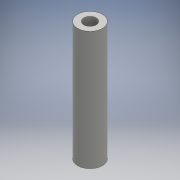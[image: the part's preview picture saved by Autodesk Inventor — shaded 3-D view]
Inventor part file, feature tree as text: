
AUTODESK INVENTOR PART (.ipt)
format: ipt  version: 2016 (Build 200138000, 138)  size: 91,648 bytes
history: native  units: mm
features: other x1, extrude x1, sketch x1
ambient origin geometry x8: Origin, YZ Plane, XZ Plane, XY Plane, X Axis, Y Axis, Z Axis, Center Point
bodies: Body1 (feature_tree)
feature tree (3):
  other  "ソリッド1"
  extrude  "押し出し1"  Depth=6.0mm
  sketch  "スケッチ1"
